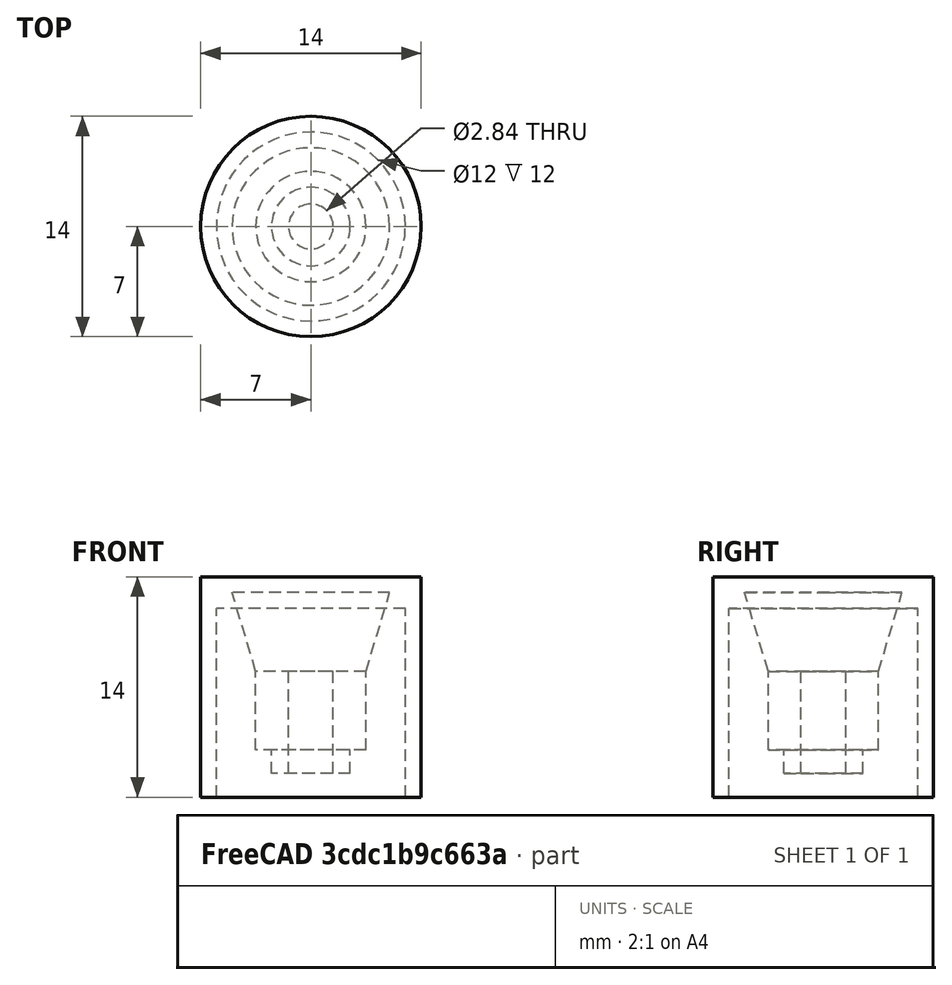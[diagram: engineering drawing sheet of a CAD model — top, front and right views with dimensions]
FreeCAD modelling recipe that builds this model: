
FCSTD DOCUMENT  (FreeCAD 0.18R16033 (Git))
Label: ceramic_standoff_test_1_cone
License: All rights reserved
LicenseURL: http://en.wikipedia.org/wiki/All_rights_reserved
objects: Part::Cylinder×5, Part::Cut×2, Part::Cone×1, Part::MultiFuse×1
note: 9 computed .brp shape members not serialized (recipe doc carries the construction recipe); baked Part::Feature solids carry a one-line shape summary decoded from their .brp

FEATURE [Part::Cylinder] Cylinder
  Angle = 360
  AttacherType = Attacher::AttachEngine3D
  Height = 8
  Placement = pos=(0,0,-3) rot=(0,0,1;0rad)
  Radius = 1.4224
  expr: Radius = 2.8448 / 2
FEATURE [Part::Cone] Cone
  Angle = 360
  AttacherType = Attacher::AttachEngine3D
  Height = 5
  Placement = pos=(0,0,5) rot=(0,0,1;0rad)
  Radius1 = 3.5
  Radius2 = 5
FEATURE [Part::Cylinder] Cylinder001
  Angle = 360
  AttacherType = Attacher::AttachEngine3D
  Height = 5
  Radius = 3.5
FEATURE [Part::Cylinder] Cylinder002
  Angle = 360
  AttacherType = Attacher::AttachEngine3D
  Height = 5
  Placement = pos=(0,0,-1.5) rot=(0,0,1;0rad)
  Radius = 2.5
FEATURE [Part::MultiFuse] Fusion
  Shapes = -> [Cylinder002,Cylinder001]
FEATURE [Part::Cut] Cut
  Base = -> Fusion
  Tool = -> Cylinder
FEATURE [Part::Cylinder] Cylinder003
  Angle = 360
  AttacherType = Attacher::AttachEngine3D
  Height = 14
  Placement = pos=(0,0,-3) rot=(0,0,1;0rad)
  Radius = 7
FEATURE [Part::Cylinder] Cylinder004
  Angle = 360
  AttacherType = Attacher::AttachEngine3D
  Height = 20
  Placement = pos=(0,0,-11) rot=(0,0,1;0rad)
  Radius = 6
FEATURE [Part::Cut] Cut001
  Base = -> Cylinder003
  Tool = -> Cylinder004
